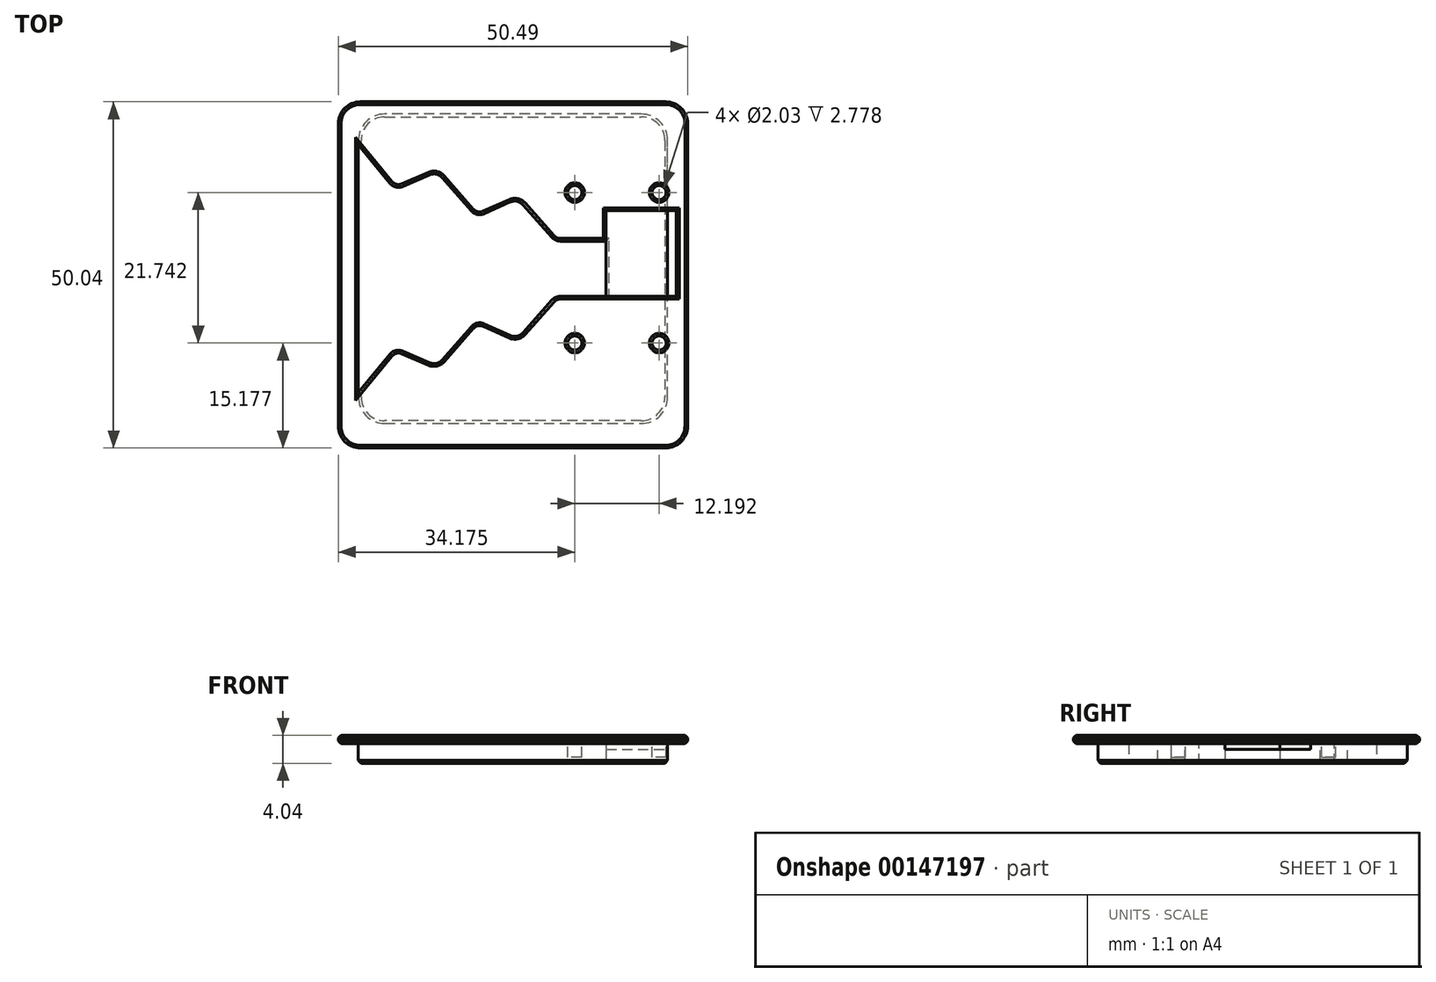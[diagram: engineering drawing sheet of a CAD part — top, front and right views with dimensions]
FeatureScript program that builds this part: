
annotation { "Feature Type Name" : "Feature", "Feature Type Description" : "" }
export const myFeature = defineFeature(function(context is Context, id is Id, definition is map)
    precondition{}
    {
        {
            var Q0;
            Q0=qCreatedBy(makeId("Top.planeOp"),FACE);
            var sketch = newSketch(context, id + "F0", { "sketchPlane" : qUnion([Q0])});
            skLineSegment(sketch, "E0", {"start": v(-8.87, 9.58) * mm, "end": v(-8.87, -1.42) * mm, "construction": true});
            skLineSegment(sketch, "E1", {"start": v(2.91, 10.58) * mm, "end": v(2.91, -5.38) * mm, "construction": true});
            skLineSegment(sketch, "E2", {"start": v(-14.2, 9.5) * mm, "end": v(-14.2, 5.06) * mm});
            skLineSegment(sketch, "E3", {"start": v(-14.2, 5.06) * mm, "end": v(-8.87, -1.42) * mm});
            skPoint(sketch, "E4.orphan", {"position": v(30.5, 9.5) * mm});
            skLineSegment(sketch, "E5", {"start": v(30.5, -12.85) * mm, "end": v(-31.2, -12.85) * mm, "construction": true});
            skLineSegment(sketch, "E6", {"start": v(-8.87, -1.42) * mm, "end": v(25.17, -12.85) * mm, "construction": true});
            skLineSegment(sketch, "E7.0", {"start": v(14.7, 10.58) * mm, "end": v(14.7, -9.34) * mm, "construction": true});
            skLineSegment(sketch, "E8.0", {"start": v(-2.86, 11.17) * mm, "end": v(-2.86, -3.44) * mm, "construction": true});
            skLineSegment(sketch, "E9", {"start": v(-8.87, -1.42) * mm, "end": v(-2.86, 1.19) * mm});
            skLineSegment(sketch, "E10", {"start": v(-2.86, 1.19) * mm, "end": v(2.91, -5.38) * mm});
            skLineSegment(sketch, "E11", {"start": v(-2.86, 1.19) * mm, "end": v(44.21, -14.62) * mm, "construction": true});
            skLineSegment(sketch, "E12.0", {"start": v(8.8, 10.58) * mm, "end": v(8.8, -7.36) * mm, "construction": true});
            skLineSegment(sketch, "E13.0", {"start": v(20.6, 10.58) * mm, "end": v(20.6, -11.32) * mm, "construction": true});
            skLineSegment(sketch, "E14.0", {"start": v(26.49, 10.58) * mm, "end": v(26.49, -12.03) * mm, "construction": true});
            skLineSegment(sketch, "E15", {"start": v(2.91, -5.38) * mm, "end": v(8.8, -2.73) * mm});
            skLineSegment(sketch, "E16", {"start": v(8.8, -2.73) * mm, "end": v(14.7, -9.34) * mm});
            skLineSegment(sketch, "E17", {"start": v(-14.2, 9.5) * mm, "end": v(30.5, 9.5) * mm});
            skLineSegment(sketch, "E18.MirrorCS", {"start": v(-14.2, -35.2) * mm, "end": v(-14.2, -30.76) * mm});
            skLineSegment(sketch, "E19.MirrorCS", {"start": v(-14.2, -35.2) * mm, "end": v(30.5, -35.2) * mm});
            skLineSegment(sketch, "E20.MirrorCS", {"start": v(30.5, -35.2) * mm, "end": v(30.5, 9.5) * mm});
            skLineSegment(sketch, "E21.MirrorCS", {"start": v(8.8, -22.97) * mm, "end": v(14.7, -16.37) * mm});
            skLineSegment(sketch, "E22.MirrorCS", {"start": v(2.91, -20.32) * mm, "end": v(8.8, -22.97) * mm});
            skLineSegment(sketch, "E23.MirrorCS", {"start": v(-2.86, -26.89) * mm, "end": v(2.91, -20.32) * mm});
            skLineSegment(sketch, "E24.MirrorCS", {"start": v(-8.87, -24.28) * mm, "end": v(-2.86, -26.89) * mm});
            skLineSegment(sketch, "E25.MirrorCS", {"start": v(-14.2, -30.76) * mm, "end": v(-8.87, -24.28) * mm});
            skLineSegment(sketch, "E26", {"start": v(14.7, -9.34) * mm, "end": v(21.6, -9.34) * mm});
            skLineSegment(sketch, "E27", {"start": v(14.7, -16.37) * mm, "end": v(21.6, -16.37) * mm});
            skLineSegment(sketch, "E28", {"start": v(21.6, -9.34) * mm, "end": v(21.6, -16.37) * mm});
            skSolve(sketch);
        }
        {
            var Q0;
            Q0 = qSketchRegion(id + "F0", true);
            extrude(context, id + "F15", {"entities" : qUnion([Q0]), "depth" : 2.82 * mm});
        }
        {
            var Q0;
            Q0=makeQuery(id+"F15.opExtrude","CAP_FACE",FACE,{"disambiguationData":[OSD([sQuery(id+"F0.wireOp",EDGE,"E2"),sQuery(id+"F0.wireOp",EDGE,"E3"),sQuery(id+"F0.wireOp",EDGE,"E9"),sQuery(id+"F0.wireOp",EDGE,"E10"),sQuery(id+"F0.wireOp",EDGE,"E15"),sQuery(id+"F0.wireOp",EDGE,"E16"),sQuery(id+"F0.wireOp",EDGE,"WPfyRJ8Z-SKz7-z9Lk-QG4x-qwaIpTsNW3Ws"),sQuery(id+"F0.wireOp",EDGE,"E17"),sQuery(id+"F0.wireOp",EDGE,"yr3Q5EQH-XaVB-AYFg-kGau-o1qB0s8Nn5HC"),sQuery(id+"F0.wireOp",EDGE,"E18.MirrorCS"),sQuery(id+"F0.wireOp",EDGE,"E19.MirrorCS"),sQuery(id+"F0.wireOp",EDGE,"E20.MirrorCS"),sQuery(id+"F0.wireOp",EDGE,"312f51c9-8ea4-499f-b14a-4c94ece54bb00.MirrorCS"),sQuery(id+"F0.wireOp",EDGE,"5ed7f7d4-c745-4085-87bf-75a65873861b0.MirrorCS"),sQuery(id+"F0.wireOp",EDGE,"E21.MirrorCS"),sQuery(id+"F0.wireOp",EDGE,"E22.MirrorCS"),sQuery(id+"F0.wireOp",EDGE,"E23.MirrorCS"),sQuery(id+"F0.wireOp",EDGE,"E24.MirrorCS"),sQuery(id+"F0.wireOp",EDGE,"E25.MirrorCS")])],"isStart":false});
            var sketch = newSketch(context, id + "F1", { "sketchPlane" : qUnion([Q0])});
            skLineSegment(sketch, "E29.0", {"start": v(-17.1, -38.76) * mm, "end": v(33.4, -38.76) * mm});
            skLineSegment(sketch, "E30.0", {"start": v(-17.1, 11.28) * mm, "end": v(33.4, 11.28) * mm});
            skLineSegment(sketch, "E31.0", {"start": v(33.4, -38.76) * mm, "end": v(33.4, 11.28) * mm});
            skLineSegment(sketch, "E32.0", {"start": v(-17.1, -38.76) * mm, "end": v(-17.1, 11.28) * mm});
            skLineSegment(sketch, "E33.0", {"start": v(-14.2, -30.76) * mm, "end": v(-8.87, -24.28) * mm});
            skLineSegment(sketch, "E34.0", {"start": v(-14.2, 5.06) * mm, "end": v(-8.87, -1.42) * mm});
            skLineSegment(sketch, "E35", {"start": v(-14.2, -30.76) * mm, "end": v(-14.2, 5.06) * mm});
            skLineSegment(sketch, "E36.0", {"start": v(-8.87, -1.42) * mm, "end": v(-2.86, 1.19) * mm});
            skLineSegment(sketch, "E37.0", {"start": v(-2.86, 1.19) * mm, "end": v(2.91, -5.38) * mm});
            skLineSegment(sketch, "E38.0", {"start": v(2.91, -20.32) * mm, "end": v(8.8, -22.97) * mm});
            skLineSegment(sketch, "E39.0", {"start": v(-2.86, -26.89) * mm, "end": v(2.91, -20.32) * mm});
            skLineSegment(sketch, "E40.0", {"start": v(-8.87, -24.28) * mm, "end": v(-2.86, -26.89) * mm});
            skLineSegment(sketch, "E41.0", {"start": v(8.8, -22.97) * mm, "end": v(14.7, -16.37) * mm});
            skLineSegment(sketch, "E42.0", {"start": v(2.91, -5.38) * mm, "end": v(8.8, -2.73) * mm});
            skLineSegment(sketch, "E43.0", {"start": v(8.8, -2.73) * mm, "end": v(14.7, -9.34) * mm});
            skLineSegment(sketch, "E44.0", {"start": v(14.7, -9.34) * mm, "end": v(21.6, -9.34) * mm});
            skLineSegment(sketch, "E45.0", {"start": v(21.6, -9.34) * mm, "end": v(21.6, -16.37) * mm});
            skLineSegment(sketch, "E46.0", {"start": v(14.7, -16.37) * mm, "end": v(21.6, -16.37) * mm});
            skSolve(sketch);
        }
        {
            var Q0;
            Q0 = qSketchRegion(id + "F1", true);
            extrude(context, id + "F2", {"entities" : qUnion([Q0]), "operationType" : NewBodyOperationType.ADD, "depth" : 1.22 * mm});
        }
        {
            var Q0;
            Q0=makeQuery(id+"F2.opExtrude","CAP_FACE",FACE,{"disambiguationData":[OSD([sQuery(id+"F1.wireOp",EDGE,"E29.0"),sQuery(id+"F1.wireOp",EDGE,"E30.0"),sQuery(id+"F1.wireOp",EDGE,"E31.0"),sQuery(id+"F1.wireOp",EDGE,"E32.0"),sQuery(id+"F1.wireOp",EDGE,"E33.0"),sQuery(id+"F1.wireOp",EDGE,"E34.0"),sQuery(id+"F1.wireOp",EDGE,"E35"),sQuery(id+"F1.wireOp",EDGE,"E36.0"),sQuery(id+"F1.wireOp",EDGE,"E37.0"),sQuery(id+"F1.wireOp",EDGE,"04cdc071-c918-469a-8fc3-3a7bfbbfa8be.0"),sQuery(id+"F1.wireOp",EDGE,"17858c4d-3210-4d10-a346-012d6d955a93.0"),sQuery(id+"F1.wireOp",EDGE,"d5eef4c5-c6c3-4fad-8fc8-3d97ba6a4ae7.0"),sQuery(id+"F1.wireOp",EDGE,"9371697a-3362-4739-8b6d-e88fbe2cb86f.0"),sQuery(id+"F1.wireOp",EDGE,"37053320-b7a5-4c68-a6f5-b0c029150e15.0"),sQuery(id+"F1.wireOp",EDGE,"2c877ff0-ef02-4ae2-9067-525089933911.0"),sQuery(id+"F1.wireOp",EDGE,"E38.0"),sQuery(id+"F1.wireOp",EDGE,"E39.0"),sQuery(id+"F1.wireOp",EDGE,"E40.0"),sQuery(id+"F1.wireOp",EDGE,"gOrJRnIJ-ag9W-5rTT-lEqP-I45cVRDarmxr")])],"isStart":false});
            var sketch = newSketch(context, id + "F3", { "sketchPlane" : qUnion([Q0])});
            skPoint(sketch, "E47.orphan", {"position": v(5.1, 13.06) * mm});
            skPoint(sketch, "E48.orphan", {"position": v(30.5, 13.06) * mm});
            skCircle(sketch, "E49", {"center": v(29.27, -1.84) * mm, "radius": 1.02 * mm});
            skCircle(sketch, "E50", {"center": v(29.27, -23.58) * mm, "radius": 1.02 * mm});
            skCircle(sketch, "E51", {"center": v(17.08, -1.84) * mm, "radius": 1.02 * mm});
            skCircle(sketch, "E52", {"center": v(17.08, -23.58) * mm, "radius": 1.02 * mm});
            skLineSegment(sketch, "E53", {"start": v(15.8, -12.71) * mm, "end": v(53.1, -12.71) * mm, "construction": true});
            skSolve(sketch);
        }
        {
            var Q0;
            Q0 = qSketchRegion(id + "F3", true);
            extrude(context, id + "F4", {"entities" : qUnion([Q0]), "operationType" : NewBodyOperationType.REMOVE, "oppositeDirection" : true, "depth" : 3.17 * mm});
        }
        {
            var Q0;
            Q0=makeQuery(id+"F15.opExtrude","CAP_FACE",FACE,{"disambiguationData":[OSD([sQuery(id+"F0.wireOp",EDGE,"E2"),sQuery(id+"F0.wireOp",EDGE,"E3"),sQuery(id+"F0.wireOp",EDGE,"E9"),sQuery(id+"F0.wireOp",EDGE,"E10"),sQuery(id+"F0.wireOp",EDGE,"E15"),sQuery(id+"F0.wireOp",EDGE,"E16"),sQuery(id+"F0.wireOp",EDGE,"E17"),sQuery(id+"F0.wireOp",EDGE,"E18.MirrorCS"),sQuery(id+"F0.wireOp",EDGE,"E19.MirrorCS"),sQuery(id+"F0.wireOp",EDGE,"E20.MirrorCS"),sQuery(id+"F0.wireOp",EDGE,"E21.MirrorCS"),sQuery(id+"F0.wireOp",EDGE,"E22.MirrorCS"),sQuery(id+"F0.wireOp",EDGE,"E23.MirrorCS"),sQuery(id+"F0.wireOp",EDGE,"E24.MirrorCS"),sQuery(id+"F0.wireOp",EDGE,"E25.MirrorCS"),sQuery(id+"F0.wireOp",EDGE,"E26"),sQuery(id+"F0.wireOp",EDGE,"E27"),sQuery(id+"F0.wireOp",EDGE,"E28")])],"isStart":true});
            var sketch = newSketch(context, id + "F5", { "sketchPlane" : qUnion([Q0])});
            skLineSegment(sketch, "E54.0", {"start": v(21.6, 16.84) * mm, "end": v(-3.93, 16.84) * mm});
            skLineSegment(sketch, "E55.0", {"start": v(21.6, 8.86) * mm, "end": v(-3.93, 8.86) * mm});
            skLineSegment(sketch, "E56", {"start": v(21.6, 16.84) * mm, "end": v(21.6, 8.86) * mm});
            skLineSegment(sketch, "E57.0", {"start": v(21.6, 9.34) * mm, "end": v(21.6, 16.37) * mm, "construction": true});
            skLineSegment(sketch, "E58", {"start": v(21.6, 12.85) * mm, "end": v(13.13, 12.85) * mm, "construction": true});
            skLineSegment(sketch, "E59", {"start": v(-3.93, 16.84) * mm, "end": v(-3.93, 8.86) * mm});
            skSolve(sketch);
        }
        {
            var Q0;
            Q0 = qSketchRegion(id + "F5", true);
            extrude(context, id + "F6", {"entities" : qUnion([Q0]), "operationType" : NewBodyOperationType.REMOVE, "endBound" : BoundingType.THROUGH_ALL, "oppositeDirection" : true, "depth" : 25.4 * mm});
        }
        {
            var Q0;
            Q0=makeQuery(id+"F2.opExtrude","CAP_FACE",FACE,{"disambiguationData":[OSD([sQuery(id+"F1.wireOp",EDGE,"E29.0"),sQuery(id+"F1.wireOp",EDGE,"E30.0"),sQuery(id+"F1.wireOp",EDGE,"E31.0"),sQuery(id+"F1.wireOp",EDGE,"E32.0"),sQuery(id+"F1.wireOp",EDGE,"E33.0"),sQuery(id+"F1.wireOp",EDGE,"E34.0"),sQuery(id+"F1.wireOp",EDGE,"E35"),sQuery(id+"F1.wireOp",EDGE,"E36.0"),sQuery(id+"F1.wireOp",EDGE,"E37.0"),sQuery(id+"F1.wireOp",EDGE,"E38.0"),sQuery(id+"F1.wireOp",EDGE,"E39.0"),sQuery(id+"F1.wireOp",EDGE,"E40.0"),sQuery(id+"F1.wireOp",EDGE,"E41.0"),sQuery(id+"F1.wireOp",EDGE,"E42.0"),sQuery(id+"F1.wireOp",EDGE,"E43.0"),sQuery(id+"F1.wireOp",EDGE,"E44.0"),sQuery(id+"F1.wireOp",EDGE,"E45.0"),sQuery(id+"F1.wireOp",EDGE,"E46.0")])],"isStart":false});
            var sketch = newSketch(context, id + "F7", { "sketchPlane" : qUnion([Q0])});
            skLineSegment(sketch, "E60", {"start": v(21.6, -12.85) * mm, "end": v(64.06, -12.85) * mm, "construction": true});
            skLineSegment(sketch, "E61.0", {"start": v(21.6, -4.47) * mm, "end": v(21.6, -16.84) * mm});
            skLineSegment(sketch, "E62.0", {"start": v(31.77, -4.47) * mm, "end": v(31.77, -16.84) * mm});
            skLineSegment(sketch, "E63", {"start": v(21.6, -16.84) * mm, "end": v(31.77, -16.84) * mm});
            skLineSegment(sketch, "E64.0", {"start": v(21.6, -4.47) * mm, "end": v(31.77, -4.47) * mm});
            skPoint(sketch, "E65.start.orphan", {"position": v(21.6, -8.86) * mm});
            skSolve(sketch);
        }
        {
            var Q0;
            Q0 = qSketchRegion(id + "F7", true);
            extrude(context, id + "F8", {"entities" : qUnion([Q0]), "operationType" : NewBodyOperationType.REMOVE, "oppositeDirection" : true, "depth" : 2.03 * mm});
        }
        {
            var Q0;
            Q0=makeQuery(id+"F15.opExtrude","SWEPT_EDGE",EDGE,{"disambiguationData":[OSD([sQuery(id+"F0.wireOp",EDGE,"E18.MirrorCS"),sQuery(id+"F0.wireOp",EDGE,"E19.MirrorCS")])]});
            var Q1;
            Q1=makeQuery(id+"F15.opExtrude","SWEPT_EDGE",EDGE,{"disambiguationData":[OSD([sQuery(id+"F0.wireOp",EDGE,"E19.MirrorCS"),sQuery(id+"F0.wireOp",EDGE,"E20.MirrorCS")])]});
            var Q2;
            Q2=makeQuery(id+"F15.opExtrude","SWEPT_EDGE",EDGE,{"disambiguationData":[OSD([sQuery(id+"F0.wireOp",EDGE,"E17"),sQuery(id+"F0.wireOp",EDGE,"E20.MirrorCS")])]});
            var Q3;
            Q3=makeQuery(id+"F15.opExtrude","SWEPT_EDGE",EDGE,{"disambiguationData":[OSD([sQuery(id+"F0.wireOp",EDGE,"E2"),sQuery(id+"F0.wireOp",EDGE,"E17")])]});
            fillet(context, id + "F9", {"entities" : qUnion([Q0, Q1, Q2, Q3]), "radius" : 3.8 * mm, "tangentPropagation" : true, "allowEdgeOverflow" : false});
        }
        {
            var Q0;
            Q0=makeQuery(id+"F2.opExtrude","SWEPT_EDGE",EDGE,{"disambiguationData":[OSD([sQuery(id+"F1.wireOp",EDGE,"E29.0"),sQuery(id+"F1.wireOp",EDGE,"E31.0")])]});
            var Q1;
            Q1=makeQuery(id+"F2.opExtrude","SWEPT_EDGE",EDGE,{"disambiguationData":[OSD([sQuery(id+"F1.wireOp",EDGE,"E30.0"),sQuery(id+"F1.wireOp",EDGE,"E31.0")])]});
            var Q2;
            Q2=makeQuery(id+"F2.opExtrude","SWEPT_EDGE",EDGE,{"disambiguationData":[OSD([sQuery(id+"F1.wireOp",EDGE,"E30.0"),sQuery(id+"F1.wireOp",EDGE,"E32.0")])]});
            var Q3;
            Q3=makeQuery(id+"F2.opExtrude","SWEPT_EDGE",EDGE,{"disambiguationData":[OSD([sQuery(id+"F1.wireOp",EDGE,"E29.0"),sQuery(id+"F1.wireOp",EDGE,"E32.0")])]});
            fillet(context, id + "F10", {"entities" : qUnion([Q0, Q1, Q2, Q3]), "radius" : 3.17 * mm, "tangentPropagation" : true, "allowEdgeOverflow" : false});
        }
        {
            var Q0;
            Q0=makeQuery(id+"F2.boolean.opBoolean","MERGE",EDGE,{"derivedFrom":[makeQuery(id+"F15.opExtrude","SWEPT_EDGE",EDGE,{"disambiguationData":[OSD([sQuery(id+"F0.wireOp",EDGE,"E24.MirrorCS"),sQuery(id+"F0.wireOp",EDGE,"E25.MirrorCS")])]}),makeQuery(id+"F2.opExtrude","SWEPT_EDGE",EDGE,{"disambiguationData":[OSD([sQuery(id+"F1.wireOp",EDGE,"E33.0"),sQuery(id+"F1.wireOp",EDGE,"E40.0")])]})]});
            var Q1;
            Q1=makeQuery(id+"F2.boolean.opBoolean","MERGE",EDGE,{"derivedFrom":[makeQuery(id+"F15.opExtrude","SWEPT_EDGE",EDGE,{"disambiguationData":[OSD([sQuery(id+"F0.wireOp",EDGE,"E22.MirrorCS"),sQuery(id+"F0.wireOp",EDGE,"E23.MirrorCS")])]}),makeQuery(id+"F2.opExtrude","SWEPT_EDGE",EDGE,{"disambiguationData":[OSD([sQuery(id+"F1.wireOp",EDGE,"E38.0"),sQuery(id+"F1.wireOp",EDGE,"E39.0")])]})]});
            var Q2;
            Q2=makeQuery(id+"F6.boolean.opBoolean","INTERSECT",EDGE,{"derivedFrom":[makeQuery(id+"F2.boolean.opBoolean","MERGE",FACE,{"derivedFrom":[makeQuery(id+"F15.opExtrude","SWEPT_FACE",FACE,{"disambiguationData":[OSD([sQuery(id+"F0.wireOp",EDGE,"E21.MirrorCS")])]}),makeQuery(id+"F2.opExtrude","SWEPT_FACE",FACE,{"disambiguationData":[OSD([sQuery(id+"F1.wireOp",EDGE,"E41.0")])]})]}),makeQuery(id+"F6.opExtrude","SWEPT_FACE",FACE,{"disambiguationData":[OSD([sQuery(id+"F5.wireOp",EDGE,"E54.0")])]})]});
            var Q3;
            Q3=makeQuery(id+"F6.boolean.opBoolean","INTERSECT",EDGE,{"derivedFrom":[makeQuery(id+"F2.boolean.opBoolean","MERGE",FACE,{"derivedFrom":[makeQuery(id+"F15.opExtrude","SWEPT_FACE",FACE,{"disambiguationData":[OSD([sQuery(id+"F0.wireOp",EDGE,"E16")])]}),makeQuery(id+"F2.opExtrude","SWEPT_FACE",FACE,{"disambiguationData":[OSD([sQuery(id+"F1.wireOp",EDGE,"E43.0")])]})]}),makeQuery(id+"F6.opExtrude","SWEPT_FACE",FACE,{"disambiguationData":[OSD([sQuery(id+"F5.wireOp",EDGE,"E55.0")])]})]});
            var Q4;
            Q4=makeQuery(id+"F2.boolean.opBoolean","MERGE",EDGE,{"derivedFrom":[makeQuery(id+"F15.opExtrude","SWEPT_EDGE",EDGE,{"disambiguationData":[OSD([sQuery(id+"F0.wireOp",EDGE,"E15"),sQuery(id+"F0.wireOp",EDGE,"E16")])]}),makeQuery(id+"F2.opExtrude","SWEPT_EDGE",EDGE,{"disambiguationData":[OSD([sQuery(id+"F1.wireOp",EDGE,"E42.0"),sQuery(id+"F1.wireOp",EDGE,"E43.0")])]})]});
            var Q5;
            Q5=makeQuery(id+"F2.boolean.opBoolean","MERGE",EDGE,{"derivedFrom":[makeQuery(id+"F15.opExtrude","SWEPT_EDGE",EDGE,{"disambiguationData":[OSD([sQuery(id+"F0.wireOp",EDGE,"E9"),sQuery(id+"F0.wireOp",EDGE,"E10")])]}),makeQuery(id+"F2.opExtrude","SWEPT_EDGE",EDGE,{"disambiguationData":[OSD([sQuery(id+"F1.wireOp",EDGE,"E36.0"),sQuery(id+"F1.wireOp",EDGE,"E37.0")])]})]});
            var Q6;
            Q6=makeQuery(id+"F2.boolean.opBoolean","MERGE",EDGE,{"derivedFrom":[makeQuery(id+"F15.opExtrude","SWEPT_EDGE",EDGE,{"disambiguationData":[OSD([sQuery(id+"F0.wireOp",EDGE,"E3"),sQuery(id+"F0.wireOp",EDGE,"E9")])]}),makeQuery(id+"F2.opExtrude","SWEPT_EDGE",EDGE,{"disambiguationData":[OSD([sQuery(id+"F1.wireOp",EDGE,"E34.0"),sQuery(id+"F1.wireOp",EDGE,"E36.0")])]})]});
            var Q7;
            Q7=makeQuery(id+"F2.boolean.opBoolean","MERGE",EDGE,{"derivedFrom":[makeQuery(id+"F15.opExtrude","SWEPT_EDGE",EDGE,{"disambiguationData":[OSD([sQuery(id+"F0.wireOp",EDGE,"E10"),sQuery(id+"F0.wireOp",EDGE,"E15")])]}),makeQuery(id+"F2.opExtrude","SWEPT_EDGE",EDGE,{"disambiguationData":[OSD([sQuery(id+"F1.wireOp",EDGE,"E37.0"),sQuery(id+"F1.wireOp",EDGE,"E42.0")])]})]});
            var Q8;
            Q8=makeQuery(id+"F2.boolean.opBoolean","MERGE",EDGE,{"derivedFrom":[makeQuery(id+"F15.opExtrude","SWEPT_EDGE",EDGE,{"disambiguationData":[OSD([sQuery(id+"F0.wireOp",EDGE,"E23.MirrorCS"),sQuery(id+"F0.wireOp",EDGE,"E24.MirrorCS")])]}),makeQuery(id+"F2.opExtrude","SWEPT_EDGE",EDGE,{"disambiguationData":[OSD([sQuery(id+"F1.wireOp",EDGE,"E39.0"),sQuery(id+"F1.wireOp",EDGE,"E40.0")])]})]});
            var Q9;
            Q9=makeQuery(id+"F2.boolean.opBoolean","MERGE",EDGE,{"derivedFrom":[makeQuery(id+"F15.opExtrude","SWEPT_EDGE",EDGE,{"disambiguationData":[OSD([sQuery(id+"F0.wireOp",EDGE,"E21.MirrorCS"),sQuery(id+"F0.wireOp",EDGE,"E22.MirrorCS")])]}),makeQuery(id+"F2.opExtrude","SWEPT_EDGE",EDGE,{"disambiguationData":[OSD([sQuery(id+"F1.wireOp",EDGE,"E38.0"),sQuery(id+"F1.wireOp",EDGE,"E41.0")])]})]});
            fillet(context, id + "F11", {"entities" : qUnion([Q0, Q1, Q2, Q3, Q4, Q5, Q6, Q7, Q8, Q9]), "radius" : 1.59 * mm, "tangentPropagation" : true, "allowEdgeOverflow" : false});
        }
        {
            var Q0;
            Q0=makeQuery(id+"F15.opExtrude","CAP_FACE",FACE,{"disambiguationData":[OSD([sQuery(id+"F0.wireOp",EDGE,"E2"),sQuery(id+"F0.wireOp",EDGE,"E3"),sQuery(id+"F0.wireOp",EDGE,"E9"),sQuery(id+"F0.wireOp",EDGE,"E10"),sQuery(id+"F0.wireOp",EDGE,"E15"),sQuery(id+"F0.wireOp",EDGE,"E16"),sQuery(id+"F0.wireOp",EDGE,"WPfyRJ8Z-SKz7-z9Lk-QG4x-qwaIpTsNW3Ws"),sQuery(id+"F0.wireOp",EDGE,"E17"),sQuery(id+"F0.wireOp",EDGE,"yr3Q5EQH-XaVB-AYFg-kGau-o1qB0s8Nn5HC"),sQuery(id+"F0.wireOp",EDGE,"E18.MirrorCS"),sQuery(id+"F0.wireOp",EDGE,"E19.MirrorCS"),sQuery(id+"F0.wireOp",EDGE,"E20.MirrorCS"),sQuery(id+"F0.wireOp",EDGE,"312f51c9-8ea4-499f-b14a-4c94ece54bb00.MirrorCS"),sQuery(id+"F0.wireOp",EDGE,"5ed7f7d4-c745-4085-87bf-75a65873861b0.MirrorCS"),sQuery(id+"F0.wireOp",EDGE,"E21.MirrorCS"),sQuery(id+"F0.wireOp",EDGE,"E22.MirrorCS"),sQuery(id+"F0.wireOp",EDGE,"E23.MirrorCS"),sQuery(id+"F0.wireOp",EDGE,"E24.MirrorCS"),sQuery(id+"F0.wireOp",EDGE,"E25.MirrorCS")])],"isStart":true});
            chamfer(context, id + "F12", {"entities" : qUnion([Q0]), "width" : 0.4 * mm, "tangentPropagation" : true});
        }
        {
            var Q0;
            Q0=makeQuery(id+"F2.opExtrude","CAP_EDGE",EDGE,{"disambiguationData":[OSD([sQuery(id+"F1.wireOp",EDGE,"E35")])],"isStart":true});
            var Q1;
            Q1=makeQuery(id+"F2.opExtrude","CAP_EDGE",EDGE,{"disambiguationData":[OSD([sQuery(id+"F1.wireOp",EDGE,"E32.0")])],"isStart":true});
            var Q2;
            {var subQ0=sQuery(id+"F1.wireOp",EDGE,"E29.0");Q2=makeQuery(id+"F2x6qbXrB5M55gE_1.opChamfer","BLEND_EDGE",EDGE,{"blendedFrom":[makeQuery(id+"F2.opExtrude","SWEPT_EDGE",EDGE,{"disambiguationData":[OSD([subQ0,sQuery(id+"F1.wireOp",EDGE,"E32.0")])]}),makeQuery(id+"F2.opExtrude","SWEPT_FACE",FACE,{"disambiguationData":[OSD([subQ0])]})],"blendedInto":[makeQuery(id+"F2.opExtrude","SWEPT_FACE",FACE,{"disambiguationData":[OSD([subQ0])]})]});}
            var Q3;
            Q3=makeQuery(id+"F2.opExtrude","CAP_EDGE",EDGE,{"disambiguationData":[OSD([sQuery(id+"F1.wireOp",EDGE,"E29.0")])],"isStart":true});
            var Q4;
            {var subQ0=sQuery(id+"F1.wireOp",EDGE,"E31.0");var subQ1=sQuery(id+"F1.wireOp",EDGE,"E29.0");Q4=makeQuery(id+"F2x6qbXrB5M55gE_1.opChamfer","BLEND_EDGE",EDGE,{"blendedFrom":[makeQuery(id+"F2.opExtrude","SWEPT_EDGE",EDGE,{"disambiguationData":[OSD([subQ1,subQ0])]}),makeQuery(id+"F2.opExtrude","CAP_FACE",FACE,{"disambiguationData":[OSD([subQ1,sQuery(id+"F1.wireOp",EDGE,"E30.0"),subQ0,sQuery(id+"F1.wireOp",EDGE,"E32.0"),sQuery(id+"F1.wireOp",EDGE,"E33.0"),sQuery(id+"F1.wireOp",EDGE,"E34.0"),sQuery(id+"F1.wireOp",EDGE,"E35"),sQuery(id+"F1.wireOp",EDGE,"E36.0"),sQuery(id+"F1.wireOp",EDGE,"E37.0"),sQuery(id+"F1.wireOp",EDGE,"04cdc071-c918-469a-8fc3-3a7bfbbfa8be.0"),sQuery(id+"F1.wireOp",EDGE,"17858c4d-3210-4d10-a346-012d6d955a93.0"),sQuery(id+"F1.wireOp",EDGE,"d5eef4c5-c6c3-4fad-8fc8-3d97ba6a4ae7.0"),sQuery(id+"F1.wireOp",EDGE,"9371697a-3362-4739-8b6d-e88fbe2cb86f.0"),sQuery(id+"F1.wireOp",EDGE,"37053320-b7a5-4c68-a6f5-b0c029150e15.0"),sQuery(id+"F1.wireOp",EDGE,"2c877ff0-ef02-4ae2-9067-525089933911.0"),sQuery(id+"F1.wireOp",EDGE,"E38.0"),sQuery(id+"F1.wireOp",EDGE,"E39.0"),sQuery(id+"F1.wireOp",EDGE,"E40.0"),sQuery(id+"F1.wireOp",EDGE,"gOrJRnIJ-ag9W-5rTT-lEqP-I45cVRDarmxr")])],"isStart":true})],"blendedInto":[makeQuery(id+"F2.opExtrude","CAP_FACE",FACE,{"disambiguationData":[OSD([subQ1,sQuery(id+"F1.wireOp",EDGE,"E30.0"),subQ0,sQuery(id+"F1.wireOp",EDGE,"E32.0"),sQuery(id+"F1.wireOp",EDGE,"E33.0"),sQuery(id+"F1.wireOp",EDGE,"E34.0"),sQuery(id+"F1.wireOp",EDGE,"E35"),sQuery(id+"F1.wireOp",EDGE,"E36.0"),sQuery(id+"F1.wireOp",EDGE,"E37.0"),sQuery(id+"F1.wireOp",EDGE,"04cdc071-c918-469a-8fc3-3a7bfbbfa8be.0"),sQuery(id+"F1.wireOp",EDGE,"17858c4d-3210-4d10-a346-012d6d955a93.0"),sQuery(id+"F1.wireOp",EDGE,"d5eef4c5-c6c3-4fad-8fc8-3d97ba6a4ae7.0"),sQuery(id+"F1.wireOp",EDGE,"9371697a-3362-4739-8b6d-e88fbe2cb86f.0"),sQuery(id+"F1.wireOp",EDGE,"37053320-b7a5-4c68-a6f5-b0c029150e15.0"),sQuery(id+"F1.wireOp",EDGE,"2c877ff0-ef02-4ae2-9067-525089933911.0"),sQuery(id+"F1.wireOp",EDGE,"E38.0"),sQuery(id+"F1.wireOp",EDGE,"E39.0"),sQuery(id+"F1.wireOp",EDGE,"E40.0"),sQuery(id+"F1.wireOp",EDGE,"gOrJRnIJ-ag9W-5rTT-lEqP-I45cVRDarmxr")])],"isStart":true})]});}
            var Q5;
            Q5=makeQuery(id+"F2.opExtrude","CAP_EDGE",EDGE,{"disambiguationData":[OSD([sQuery(id+"F1.wireOp",EDGE,"E31.0")])],"isStart":true});
            var Q6;
            {var subQ0=sQuery(id+"F1.wireOp",EDGE,"E32.0");var subQ1=sQuery(id+"F1.wireOp",EDGE,"E30.0");Q6=makeQuery(id+"F2x6qbXrB5M55gE_1.opChamfer","BLEND_EDGE",EDGE,{"blendedFrom":[makeQuery(id+"F2.opExtrude","SWEPT_EDGE",EDGE,{"disambiguationData":[OSD([subQ1,subQ0])]}),makeQuery(id+"F2.opExtrude","CAP_FACE",FACE,{"disambiguationData":[OSD([sQuery(id+"F1.wireOp",EDGE,"E29.0"),subQ1,sQuery(id+"F1.wireOp",EDGE,"E31.0"),subQ0,sQuery(id+"F1.wireOp",EDGE,"E33.0"),sQuery(id+"F1.wireOp",EDGE,"E34.0"),sQuery(id+"F1.wireOp",EDGE,"E35"),sQuery(id+"F1.wireOp",EDGE,"E36.0"),sQuery(id+"F1.wireOp",EDGE,"E37.0"),sQuery(id+"F1.wireOp",EDGE,"04cdc071-c918-469a-8fc3-3a7bfbbfa8be.0"),sQuery(id+"F1.wireOp",EDGE,"17858c4d-3210-4d10-a346-012d6d955a93.0"),sQuery(id+"F1.wireOp",EDGE,"d5eef4c5-c6c3-4fad-8fc8-3d97ba6a4ae7.0"),sQuery(id+"F1.wireOp",EDGE,"9371697a-3362-4739-8b6d-e88fbe2cb86f.0"),sQuery(id+"F1.wireOp",EDGE,"37053320-b7a5-4c68-a6f5-b0c029150e15.0"),sQuery(id+"F1.wireOp",EDGE,"2c877ff0-ef02-4ae2-9067-525089933911.0"),sQuery(id+"F1.wireOp",EDGE,"E38.0"),sQuery(id+"F1.wireOp",EDGE,"E39.0"),sQuery(id+"F1.wireOp",EDGE,"E40.0"),sQuery(id+"F1.wireOp",EDGE,"gOrJRnIJ-ag9W-5rTT-lEqP-I45cVRDarmxr")])],"isStart":true})],"blendedInto":[makeQuery(id+"F2.opExtrude","CAP_FACE",FACE,{"disambiguationData":[OSD([sQuery(id+"F1.wireOp",EDGE,"E29.0"),subQ1,sQuery(id+"F1.wireOp",EDGE,"E31.0"),subQ0,sQuery(id+"F1.wireOp",EDGE,"E33.0"),sQuery(id+"F1.wireOp",EDGE,"E34.0"),sQuery(id+"F1.wireOp",EDGE,"E35"),sQuery(id+"F1.wireOp",EDGE,"E36.0"),sQuery(id+"F1.wireOp",EDGE,"E37.0"),sQuery(id+"F1.wireOp",EDGE,"04cdc071-c918-469a-8fc3-3a7bfbbfa8be.0"),sQuery(id+"F1.wireOp",EDGE,"17858c4d-3210-4d10-a346-012d6d955a93.0"),sQuery(id+"F1.wireOp",EDGE,"d5eef4c5-c6c3-4fad-8fc8-3d97ba6a4ae7.0"),sQuery(id+"F1.wireOp",EDGE,"9371697a-3362-4739-8b6d-e88fbe2cb86f.0"),sQuery(id+"F1.wireOp",EDGE,"37053320-b7a5-4c68-a6f5-b0c029150e15.0"),sQuery(id+"F1.wireOp",EDGE,"2c877ff0-ef02-4ae2-9067-525089933911.0"),sQuery(id+"F1.wireOp",EDGE,"E38.0"),sQuery(id+"F1.wireOp",EDGE,"E39.0"),sQuery(id+"F1.wireOp",EDGE,"E40.0"),sQuery(id+"F1.wireOp",EDGE,"gOrJRnIJ-ag9W-5rTT-lEqP-I45cVRDarmxr")])],"isStart":true})]});}
            var Q7;
            Q7=makeQuery(id+"F2.opExtrude","CAP_EDGE",EDGE,{"disambiguationData":[OSD([sQuery(id+"F1.wireOp",EDGE,"E30.0")])],"isStart":true});
            var Q8;
            {var subQ0=sQuery(id+"F1.wireOp",EDGE,"E31.0");var subQ1=sQuery(id+"F1.wireOp",EDGE,"E30.0");Q8=makeQuery(id+"F2x6qbXrB5M55gE_1.opChamfer","BLEND_EDGE",EDGE,{"blendedFrom":[makeQuery(id+"F2.opExtrude","SWEPT_EDGE",EDGE,{"disambiguationData":[OSD([subQ1,subQ0])]}),makeQuery(id+"F2.opExtrude","CAP_FACE",FACE,{"disambiguationData":[OSD([sQuery(id+"F1.wireOp",EDGE,"E29.0"),subQ1,subQ0,sQuery(id+"F1.wireOp",EDGE,"E32.0"),sQuery(id+"F1.wireOp",EDGE,"E33.0"),sQuery(id+"F1.wireOp",EDGE,"E34.0"),sQuery(id+"F1.wireOp",EDGE,"E35"),sQuery(id+"F1.wireOp",EDGE,"E36.0"),sQuery(id+"F1.wireOp",EDGE,"E37.0"),sQuery(id+"F1.wireOp",EDGE,"04cdc071-c918-469a-8fc3-3a7bfbbfa8be.0"),sQuery(id+"F1.wireOp",EDGE,"17858c4d-3210-4d10-a346-012d6d955a93.0"),sQuery(id+"F1.wireOp",EDGE,"d5eef4c5-c6c3-4fad-8fc8-3d97ba6a4ae7.0"),sQuery(id+"F1.wireOp",EDGE,"9371697a-3362-4739-8b6d-e88fbe2cb86f.0"),sQuery(id+"F1.wireOp",EDGE,"37053320-b7a5-4c68-a6f5-b0c029150e15.0"),sQuery(id+"F1.wireOp",EDGE,"2c877ff0-ef02-4ae2-9067-525089933911.0"),sQuery(id+"F1.wireOp",EDGE,"E38.0"),sQuery(id+"F1.wireOp",EDGE,"E39.0"),sQuery(id+"F1.wireOp",EDGE,"E40.0"),sQuery(id+"F1.wireOp",EDGE,"gOrJRnIJ-ag9W-5rTT-lEqP-I45cVRDarmxr")])],"isStart":true})],"blendedInto":[makeQuery(id+"F2.opExtrude","CAP_FACE",FACE,{"disambiguationData":[OSD([sQuery(id+"F1.wireOp",EDGE,"E29.0"),subQ1,subQ0,sQuery(id+"F1.wireOp",EDGE,"E32.0"),sQuery(id+"F1.wireOp",EDGE,"E33.0"),sQuery(id+"F1.wireOp",EDGE,"E34.0"),sQuery(id+"F1.wireOp",EDGE,"E35"),sQuery(id+"F1.wireOp",EDGE,"E36.0"),sQuery(id+"F1.wireOp",EDGE,"E37.0"),sQuery(id+"F1.wireOp",EDGE,"04cdc071-c918-469a-8fc3-3a7bfbbfa8be.0"),sQuery(id+"F1.wireOp",EDGE,"17858c4d-3210-4d10-a346-012d6d955a93.0"),sQuery(id+"F1.wireOp",EDGE,"d5eef4c5-c6c3-4fad-8fc8-3d97ba6a4ae7.0"),sQuery(id+"F1.wireOp",EDGE,"9371697a-3362-4739-8b6d-e88fbe2cb86f.0"),sQuery(id+"F1.wireOp",EDGE,"37053320-b7a5-4c68-a6f5-b0c029150e15.0"),sQuery(id+"F1.wireOp",EDGE,"2c877ff0-ef02-4ae2-9067-525089933911.0"),sQuery(id+"F1.wireOp",EDGE,"E38.0"),sQuery(id+"F1.wireOp",EDGE,"E39.0"),sQuery(id+"F1.wireOp",EDGE,"E40.0"),sQuery(id+"F1.wireOp",EDGE,"gOrJRnIJ-ag9W-5rTT-lEqP-I45cVRDarmxr")])],"isStart":true})]});}
            chamfer(context, id + "F13", {"entities" : qUnion([Q0, Q1, Q2, Q3, Q4, Q5, Q6, Q7, Q8]), "width" : 0.4 * mm, "tangentPropagation" : true});
        }
        {
            var Q0;
            Q0=makeQuery(id+"F2.opExtrude","CAP_FACE",FACE,{"disambiguationData":[OSD([sQuery(id+"F1.wireOp",EDGE,"E29.0"),sQuery(id+"F1.wireOp",EDGE,"E30.0"),sQuery(id+"F1.wireOp",EDGE,"E31.0"),sQuery(id+"F1.wireOp",EDGE,"E32.0"),sQuery(id+"F1.wireOp",EDGE,"E33.0"),sQuery(id+"F1.wireOp",EDGE,"E34.0"),sQuery(id+"F1.wireOp",EDGE,"E35"),sQuery(id+"F1.wireOp",EDGE,"E36.0"),sQuery(id+"F1.wireOp",EDGE,"E37.0"),sQuery(id+"F1.wireOp",EDGE,"04cdc071-c918-469a-8fc3-3a7bfbbfa8be.0"),sQuery(id+"F1.wireOp",EDGE,"17858c4d-3210-4d10-a346-012d6d955a93.0"),sQuery(id+"F1.wireOp",EDGE,"9371697a-3362-4739-8b6d-e88fbe2cb86f.0"),sQuery(id+"F1.wireOp",EDGE,"37053320-b7a5-4c68-a6f5-b0c029150e15.0"),sQuery(id+"F1.wireOp",EDGE,"2c877ff0-ef02-4ae2-9067-525089933911.0"),sQuery(id+"F1.wireOp",EDGE,"E38.0"),sQuery(id+"F1.wireOp",EDGE,"E39.0"),sQuery(id+"F1.wireOp",EDGE,"E40.0"),sQuery(id+"F1.wireOp",EDGE,"f7a11299-c911-4259-9688-c06d5c3ec539.0"),sQuery(id+"F1.wireOp",EDGE,"9518898d-ff48-4218-9d8c-dbcac31c1cf3.0")])],"isStart":false});
            chamfer(context, id + "F14", {"entities" : qUnion([Q0]), "width" : 0.4 * mm, "tangentPropagation" : true});
        }
    });
